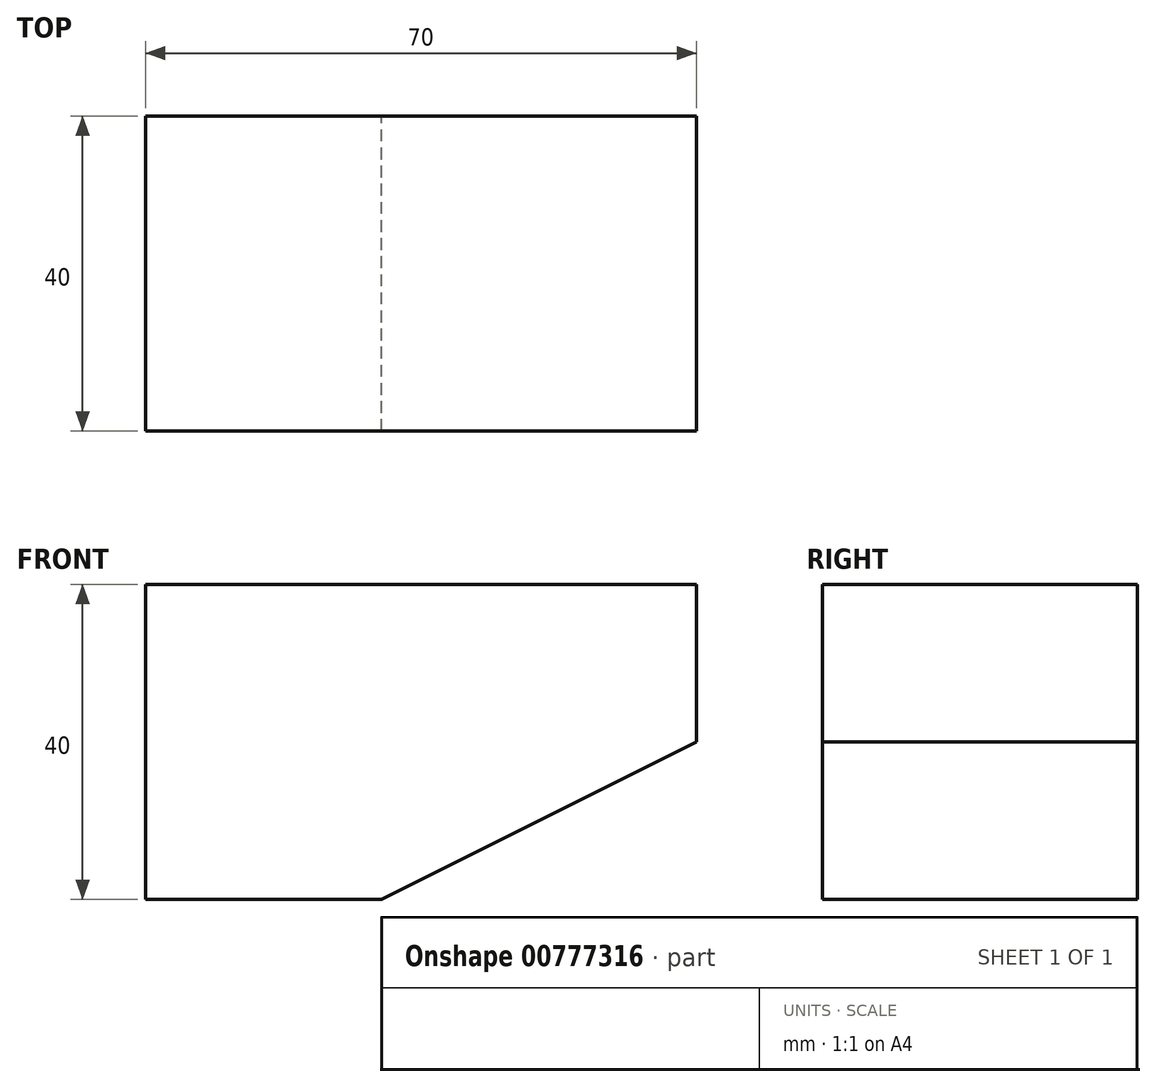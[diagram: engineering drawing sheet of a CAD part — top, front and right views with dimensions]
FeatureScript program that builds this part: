
annotation { "Feature Type Name" : "Feature", "Feature Type Description" : "" }
export const myFeature = defineFeature(function(context is Context, id is Id, definition is map)
    precondition{}
    {
        {
            var Q0;
            Q0=qCreatedBy(makeId("Front.planeOp"),FACE);
            var sketch = newSketch(context, id + "F0", { "sketchPlane" : qUnion([Q0])});
            skLineSegment(sketch, "E0.bottom", {"start": v(0, 46.37) * mm, "end": v(70, 46.37) * mm});
            skLineSegment(sketch, "E0.top", {"start": v(0, 6.37) * mm, "end": v(70, 6.37) * mm});
            skLineSegment(sketch, "E0.left", {"start": v(0, 46.37) * mm, "end": v(0, 6.37) * mm});
            skLineSegment(sketch, "E0.right", {"start": v(70, 46.37) * mm, "end": v(70, 6.37) * mm});
            skLineSegment(sketch, "E1", {"start": v(0, 6.37) * mm, "end": v(30, 6.37) * mm});
            skLineSegment(sketch, "E2", {"start": v(70, 46.37) * mm, "end": v(70, 26.37) * mm});
            skLineSegment(sketch, "E3", {"start": v(30, 6.37) * mm, "end": v(70, 26.37) * mm});
            skSolve(sketch);
        }
        {
            var Q0;
            Q0=makeQuery(id+"F0.imprint","IMPRINT",FACE,{"disambiguationData":[TD([[makeQuery(id+"F0.imprint","IMPRINT",EDGE,{"derivedFrom":sQuery(id+"F0.wireOp",EDGE,"E0.bottom")}),-1.0]])]});
            extrude(context, id + "F1", {"entities" : qUnion([Q0]), "depth" : 40 * mm, "offsetDistance" : 25 * mm});
        }
    });
